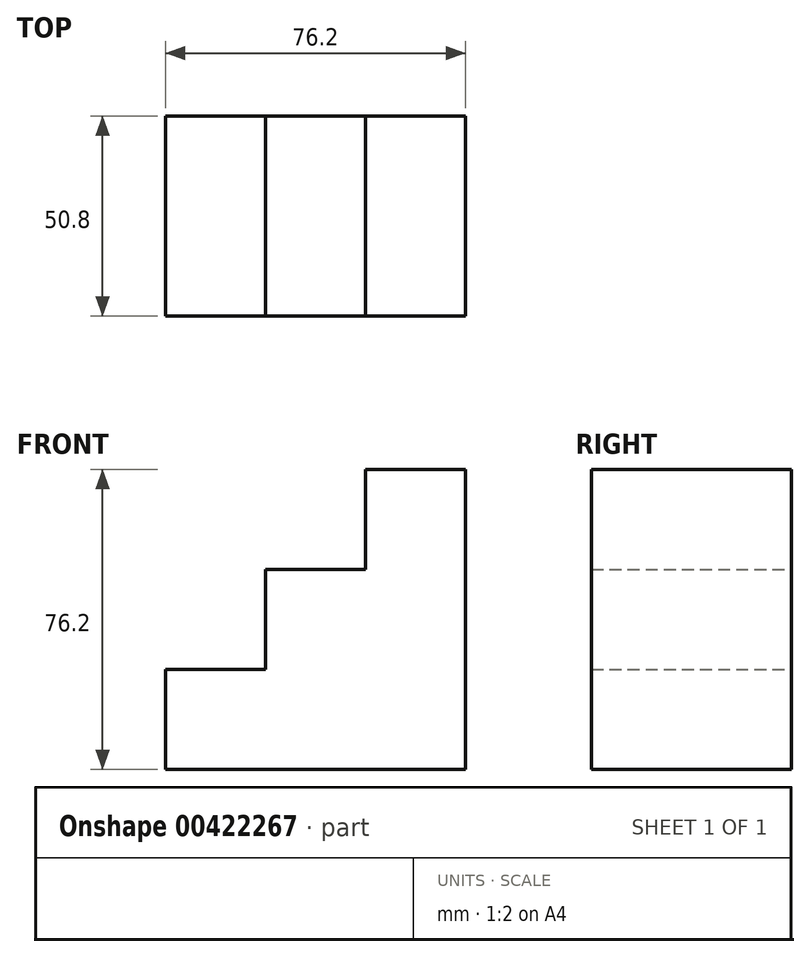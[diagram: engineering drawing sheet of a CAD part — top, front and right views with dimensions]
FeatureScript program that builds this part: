
annotation { "Feature Type Name" : "Feature", "Feature Type Description" : "" }
export const myFeature = defineFeature(function(context is Context, id is Id, definition is map)
    precondition{}
    {
        {
            var Q0;
            Q0=qCreatedBy(makeId("Front.planeOp"),FACE);
            var sketch = newSketch(context, id + "F0", { "sketchPlane" : qUnion([Q0])});
            skLineSegment(sketch, "E0", {"start": v(0, 0) * mm, "end": v(-76.2, 0) * mm});
            skLineSegment(sketch, "E1", {"start": v(-76.2, 0) * mm, "end": v(-76.2, 25.4) * mm});
            skLineSegment(sketch, "E2", {"start": v(-76.2, 25.4) * mm, "end": v(-50.8, 25.4) * mm});
            skLineSegment(sketch, "E3", {"start": v(-50.8, 25.4) * mm, "end": v(-50.8, 50.8) * mm});
            skLineSegment(sketch, "E4", {"start": v(-50.8, 50.8) * mm, "end": v(-25.4, 50.8) * mm});
            skLineSegment(sketch, "E5", {"start": v(-25.4, 50.8) * mm, "end": v(-25.4, 76.2) * mm});
            skLineSegment(sketch, "E6", {"start": v(-25.4, 76.2) * mm, "end": v(0, 76.2) * mm});
            skLineSegment(sketch, "E7", {"start": v(0, 76.2) * mm, "end": v(0, -1.52) * mm});
            skSolve(sketch);
        }
        {
            var Q0;
            {var subQ0=sQuery(id+"F0.wireOp",EDGE,"E0");Q0=makeQuery(id+"F0.imprint","IMPRINT",FACE,{"disambiguationData":[TD([[makeQuery(id+"F0.imprint","IMPRINT",EDGE,{"derivedFrom":subQ0}),-1.0]])]});}
            extrude(context, id + "F1", {"entities" : qUnion([Q0]), "depth" : 50.8 * mm});
        }
    });
